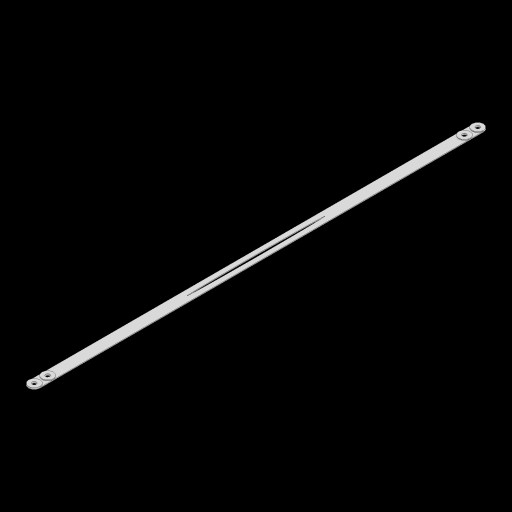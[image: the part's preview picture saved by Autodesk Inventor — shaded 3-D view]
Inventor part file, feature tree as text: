
AUTODESK INVENTOR PART (.ipt)
format: ipt  version: 2023 (Build 270158000, 158)  size: 119,808 bytes
history: native  units: mm
features: extrude x2, sketch x1
ambient origin geometry x8: Origin, YZ Plane, XZ Plane, XY Plane, X Axis, Y Axis, Z Axis, Center Point
bodies: Solid1 (feature_tree)
feature tree (3):
  sketch  "Sketch1"  dims[d0=273.901mm d1=90.0deg d2=45.9mm d3=273.901mm d4=90.0deg d5=15.0mm d6=15.0mm d7=2.5mm d8=15.0mm d9=5.5mm d10=5.5mm d11=1.0mm d12=0.0mm d13=2.0mm d14=0.0mm d15=3.0mm]
  extrude  "Extrusion1"  TaperAngle=90.0deg  [1 undecoded]
  extrude  "Extrusion2"  Depth=2.0mm
note: 1 required parameter value undecoded (feature->parameter linkage not recoverable at this tier; creation-order binding heuristic only, values carry confidence <= 0.55)
